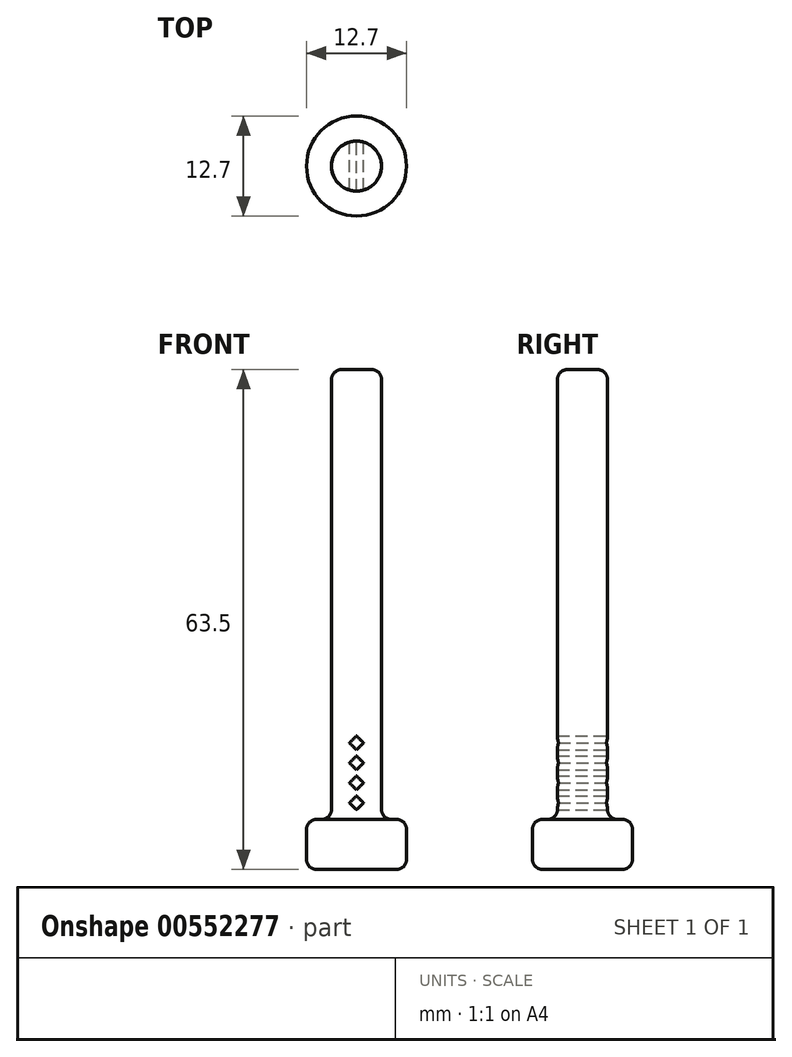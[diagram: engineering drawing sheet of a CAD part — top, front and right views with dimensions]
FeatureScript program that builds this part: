
annotation { "Feature Type Name" : "Feature", "Feature Type Description" : "" }
export const myFeature = defineFeature(function(context is Context, id is Id, definition is map)
    precondition{}
    {
        {
            var Q0;
            Q0=qCreatedBy(makeId("Top.planeOp"),FACE);
            var sketch = newSketch(context, id + "F0", { "sketchPlane" : qUnion([Q0])});
            skCircle(sketch, "E0", {"center": v(0, 0) * mm, "radius": 6.35 * mm});
            skCircle(sketch, "E1", {"center": v(0, 0) * mm, "radius": 3.18 * mm});
            skSolve(sketch);
        }
        {
            var Q0;
            Q0=makeQuery(id+"F0.imprint","IMPRINT",FACE,{"disambiguationData":[TD([[makeQuery(id+"F0.imprint","IMPRINT",EDGE,{"derivedFrom":sQuery(id+"F0.wireOp",EDGE,"E0")}),1.0]])]});
            var Q1;
            Q1=makeQuery(id+"F0.imprint","IMPRINT",FACE,{"disambiguationData":[TD([[makeQuery(id+"F0.imprint","IMPRINT",EDGE,{"derivedFrom":sQuery(id+"F0.wireOp",EDGE,"E1")}),1.0]])]});
            extrude(context, id + "F1", {"entities" : qUnion([Q0, Q1]), "depth" : 6.35 * mm, "offsetDistance" : 25.4 * mm});
        }
        {
            var Q0;
            Q0=makeQuery(id+"F0.imprint","IMPRINT",FACE,{"disambiguationData":[TD([[makeQuery(id+"F0.imprint","IMPRINT",EDGE,{"derivedFrom":sQuery(id+"F0.wireOp",EDGE,"E1")}),1.0]])]});
            extrude(context, id + "F2", {"entities" : qUnion([Q0]), "operationType" : NewBodyOperationType.ADD, "depth" : 63.5 * mm, "offsetDistance" : 25.4 * mm});
        }
        {
            var Q0;
            Q0=qCreatedBy(makeId("Front.planeOp"),FACE);
            var sketch = newSketch(context, id + "F3", { "sketchPlane" : qUnion([Q0])});
            skLineSegment(sketch, "E2", {"start": v(0, 0) * mm, "end": v(0, 31.45) * mm, "construction": true});
            skLineSegment(sketch, "E3.bottom", {"start": v(0.9, 8.46) * mm, "end": v(0, 9.36) * mm});
            skLineSegment(sketch, "E3.top", {"start": v(0, 7.56) * mm, "end": v(-0.9, 8.46) * mm});
            skLineSegment(sketch, "E3.left", {"start": v(0.9, 8.46) * mm, "end": v(0, 7.56) * mm});
            skLineSegment(sketch, "E3.right", {"start": v(0, 9.36) * mm, "end": v(-0.9, 8.46) * mm});
            skPoint(sketch, "E3.middle", {"position": v(0, 8.46) * mm});
            skLineSegment(sketch, "E4.0.1.0", {"start": v(0, 11.9) * mm, "end": v(-0.9, 11) * mm});
            skLineSegment(sketch, "E4.0.1.1", {"start": v(0.9, 11) * mm, "end": v(0, 10.1) * mm});
            skLineSegment(sketch, "E4.0.1.2", {"start": v(0, 10.1) * mm, "end": v(-0.9, 11) * mm});
            skLineSegment(sketch, "E4.0.1.3", {"start": v(0.9, 11) * mm, "end": v(0, 11.9) * mm});
            skPoint(sketch, "E4.0.1.4", {"position": v(0, 11) * mm});
            skLineSegment(sketch, "E4.0.2.0", {"start": v(0, 14.44) * mm, "end": v(-0.9, 13.54) * mm});
            skLineSegment(sketch, "E4.0.2.1", {"start": v(0.9, 13.54) * mm, "end": v(0, 12.64) * mm});
            skLineSegment(sketch, "E4.0.2.2", {"start": v(0, 12.64) * mm, "end": v(-0.9, 13.54) * mm});
            skLineSegment(sketch, "E4.0.2.3", {"start": v(0.9, 13.54) * mm, "end": v(0, 14.44) * mm});
            skPoint(sketch, "E4.0.2.4", {"position": v(0, 13.54) * mm});
            skLineSegment(sketch, "E4.0.3.0", {"start": v(0, 16.98) * mm, "end": v(-0.9, 16.08) * mm});
            skLineSegment(sketch, "E4.0.3.1", {"start": v(0.9, 16.08) * mm, "end": v(0, 15.18) * mm});
            skLineSegment(sketch, "E4.0.3.2", {"start": v(0, 15.18) * mm, "end": v(-0.9, 16.08) * mm});
            skLineSegment(sketch, "E4.0.3.3", {"start": v(0.9, 16.08) * mm, "end": v(0, 16.98) * mm});
            skPoint(sketch, "E4.0.3.4", {"position": v(0, 16.08) * mm});
            skLineSegment(sketch, "E4.direction1", {"start": v(0, 7.56) * mm, "end": v(25.4, 7.56) * mm, "construction": true});
            skLineSegment(sketch, "E4.direction2", {"start": v(0, 7.56) * mm, "end": v(0, 10.1) * mm, "construction": true});
            skSolve(sketch);
        }
        {
            var Q0;
            Q0 = qSketchRegion(id + "F3", true);
            extrude(context, id + "F4", {"entities" : qUnion([Q0]), "operationType" : NewBodyOperationType.REMOVE, "endBound" : BoundingType.SYMMETRIC, "depth" : 25.4 * mm, "offsetDistance" : 25.4 * mm, "hasSecondDirection" : true, "secondDirectionOppositeDirection" : true, "secondDirectionDepth" : 25.4 * mm});
        }
        {
            var Q0;
            Q0=makeQuery(id+"F2.opExtrude","CAP_EDGE",EDGE,{"disambiguationData":[OSD([sQuery(id+"F0.wireOp",EDGE,"E1")])],"isStart":false});
            var Q1;
            Q1=makeQuery(id+"F2.boolean.opBoolean","INTERSECT",EDGE,{"derivedFrom":[makeQuery(id+"F1.opExtrude","CAP_FACE",FACE,{"disambiguationData":[OSD([sQuery(id+"F0.wireOp",EDGE,"E0")])],"isStart":false}),makeQuery(id+"F2.opExtrude","SWEPT_FACE",FACE,{"disambiguationData":[OSD([sQuery(id+"F0.wireOp",EDGE,"E1")])]})]});
            var Q2;
            Q2=makeQuery(id+"F1.opExtrude","CAP_EDGE",EDGE,{"disambiguationData":[OSD([sQuery(id+"F0.wireOp",EDGE,"E0")])],"isStart":false});
            var Q3;
            Q3=makeQuery(id+"F1.opExtrude","CAP_EDGE",EDGE,{"disambiguationData":[OSD([sQuery(id+"F0.wireOp",EDGE,"E0")])],"isStart":true});
            fillet(context, id + "F5", {"entities" : qUnion([Q0, Q1, Q2, Q3]), "radius" : 1.27 * mm, "tangentPropagation" : true, "allowEdgeOverflow" : false});
        }
    });
